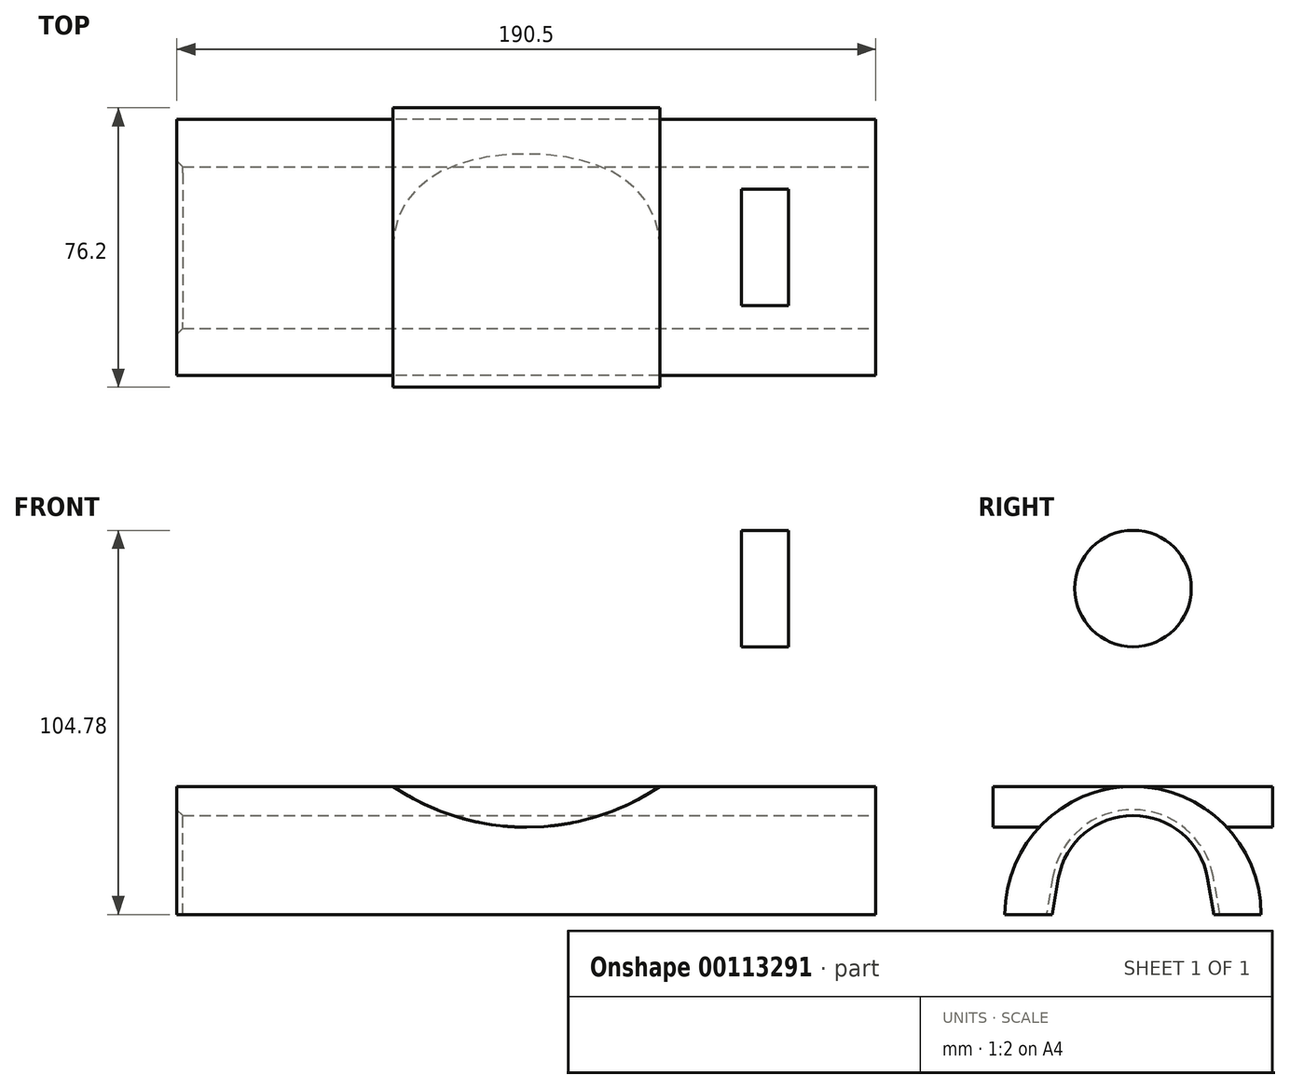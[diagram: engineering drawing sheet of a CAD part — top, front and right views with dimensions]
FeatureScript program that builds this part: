
annotation { "Feature Type Name" : "Feature", "Feature Type Description" : "" }
export const myFeature = defineFeature(function(context is Context, id is Id, definition is map)
    precondition{}
    {
        {
            var Q0;
            Q0=qCreatedBy(makeId("Top.planeOp"),FACE);
            var sketch = newSketch(context, id + "F0", { "sketchPlane" : qUnion([Q0])});
            skLineSegment(sketch, "E0.bottom", {"start": v(95.25, 34.92) * mm, "end": v(-95.25, 34.92) * mm});
            skLineSegment(sketch, "E0.top", {"start": v(95.25, -34.93) * mm, "end": v(-95.25, -34.93) * mm});
            skLineSegment(sketch, "E0.left", {"start": v(95.25, 34.93) * mm, "end": v(95.25, -34.93) * mm});
            skLineSegment(sketch, "E0.right", {"start": v(-95.25, 34.93) * mm, "end": v(-95.25, -34.93) * mm});
            skPoint(sketch, "E0.middle", {"position": v(0, 0) * mm});
            skSolve(sketch);
        }
        {
            var Q0;
            Q0=makeQuery(id+"F0.imprint","IMPRINT",FACE,{"disambiguationData":[TD([[makeQuery(id+"F0.imprint","IMPRINT",EDGE,{"derivedFrom":sQuery(id+"F0.wireOp",EDGE,"E0.bottom")}),1.0]])]});
            extrude(context, id + "F1", {"entities" : qUnion([Q0]), "depth" : 34.92 * mm});
        }
        {
            var Q0;
            Q0=makeQuery(id+"F1.opExtrude","SWEPT_FACE",FACE,{"disambiguationData":[OSD([sQuery(id+"F0.wireOp",EDGE,"E0.left")])]});
            var sketch = newSketch(context, id + "F2", { "sketchPlane" : qUnion([Q0])});
            skCircle(sketch, "E1", {"center": v(0, 0) * mm, "radius": 34.93 * mm});
            skSolve(sketch);
        }
        {
            var Q0;
            Q0=makeQuery(id+"F1.opExtrude","SWEPT_FACE",FACE,{"disambiguationData":[OSD([sQuery(id+"F0.wireOp",EDGE,"E0.top")])]});
            var sketch = newSketch(context, id + "F3", { "sketchPlane" : qUnion([Q0])});
            skLineSegment(sketch, "E2", {"start": v(0, 0) * mm, "end": v(0, 88.9) * mm});
            skCircle(sketch, "E3", {"center": v(0, 88.9) * mm, "radius": 65.09 * mm});
            skSolve(sketch);
        }
        {
            var Q0;
            {var subQ1=sQuery(id+"F0.wireOp",EDGE,"E0.left");var subQ2=makeQuery(id+"F1.opExtrude","SWEPT_EDGE",EDGE,{"disambiguationData":[OSD([sQuery(id+"F0.wireOp",EDGE,"E0.top"),subQ1])]});Q0=makeQuery(id+"F2.imprint","IMPRINT",FACE,{"disambiguationData":[TD([[makeQuery(id+"F2.imprint","IMPRINT",EDGE,{"derivedFrom":subQ2}),1.0]])]});}
            var Q1;
            {var subQ1=sQuery(id+"F0.wireOp",EDGE,"E0.left");var subQ2=makeQuery(id+"F1.opExtrude","SWEPT_EDGE",EDGE,{"disambiguationData":[OSD([sQuery(id+"F0.wireOp",EDGE,"E0.bottom"),subQ1])]});Q1=makeQuery(id+"F2.imprint","IMPRINT",FACE,{"disambiguationData":[TD([[makeQuery(id+"F2.imprint","IMPRINT",EDGE,{"derivedFrom":subQ2}),-1.0]])]});}
            extrude(context, id + "F4", {"entities" : qUnion([Q0, Q1]), "operationType" : NewBodyOperationType.REMOVE, "oppositeDirection" : true, "depth" : 190.5 * mm});
        }
        {
            var Q0;
            {var subQ0=sQuery(id+"F3.wireOp",EDGE,"E3");var subQ1=makeQuery(id+"F1.opExtrude","CAP_EDGE",EDGE,{"disambiguationData":[OSD([sQuery(id+"F0.wireOp",EDGE,"E0.top")])],"isStart":false});var subQ2=makeQuery(id+"F3.imprint","INTERSECT",VERTEX,{"disambiguationData":[OD(0.0)],"derivedFrom":[subQ1,subQ0]});Q0=makeQuery(id+"F3.imprint","IMPRINT",FACE,{"disambiguationData":[TD([[makeQuery(id+"F3.imprint","IMPRINT",EDGE,{"disambiguationData":[TD([[subQ2,1.0]])],"derivedFrom":subQ0}),1.0]])]});}
            var Q1;
            {var subQ0=sQuery(id+"F3.wireOp",EDGE,"E3");var subQ1=sQuery(id+"F3.wireOp",EDGE,"E2");var subQ2=makeQuery(id+"F3.imprint","INTERSECT",VERTEX,{"derivedFrom":[subQ1,subQ0]});Q1=makeQuery(id+"F3.imprint","IMPRINT",FACE,{"disambiguationData":[TD([[makeQuery(id+"F3.imprint","IMPRINT",EDGE,{"disambiguationData":[TD([[subQ2,-1.0]])],"derivedFrom":subQ1}),-1.0]])]});}
            var Q2;
            {var subQ0=sQuery(id+"F3.wireOp",EDGE,"E3");var subQ1=sQuery(id+"F3.wireOp",EDGE,"E2");var subQ2=makeQuery(id+"F3.imprint","INTERSECT",VERTEX,{"derivedFrom":[subQ1,subQ0]});Q2=makeQuery(id+"F3.imprint","IMPRINT",FACE,{"disambiguationData":[TD([[makeQuery(id+"F3.imprint","IMPRINT",EDGE,{"disambiguationData":[TD([[subQ2,-1.0]])],"derivedFrom":subQ1}),1.0]])]});}
            extrude(context, id + "F5", {"entities" : qUnion([Q0, Q1, Q2]), "operationType" : NewBodyOperationType.ADD, "oppositeDirection" : true, "depth" : 73.02 * mm});
        }
        {
            var Q0;
            Q0=makeQuery(id+"F5.opExtrude","CAP_FACE",FACE,{"disambiguationData":[OSD([sQuery(id+"F3.wireOp",EDGE,"E3")])],"isStart":true});
            extrude(context, id + "F6", {"entities" : qUnion([Q0]), "operationType" : NewBodyOperationType.ADD, "depth" : 3.17 * mm});
        }
        {
            var Q0;
            Q0=makeQuery(id+"F1.opExtrude","SWEPT_FACE",FACE,{"disambiguationData":[OSD([sQuery(id+"F0.wireOp",EDGE,"E0.left")])]});
            var sketch = newSketch(context, id + "F7", { "sketchPlane" : qUnion([Q0])});
            skPoint(sketch, "E4", {"position": v(0, 0) * mm});
            skSolve(sketch);
        }
        {
            var Q0;
            {var subQ0=sQuery(id+"F0.wireOp",EDGE,"E0.left");var subQ1=makeQuery(id+"F1.opExtrude","CAP_EDGE",EDGE,{"disambiguationData":[OSD([subQ0])],"isStart":true});Q0=makeQuery(id+"F7.imprint","IMPRINT",FACE,{"disambiguationData":[TD([[makeQuery(id+"F7.imprint","IMPRINT",EDGE,{"derivedFrom":subQ1}),-1.0]])]});}
            var sketch = newSketch(context, id + "F8", { "sketchPlane" : qUnion([Q0])});
            skPoint(sketch, "E5", {"position": v(0, 0) * mm});
            skLineSegment(sketch, "E6", {"start": v(0, 0) * mm, "end": v(0, 6.35) * mm});
            skArc(sketch, "E7", {"start": v(20.32, 9.93) * mm, "mid": v(0, 26.99) * mm, "end": v(-20.32, 9.93) * mm});
            skArc(sketch, "E8", {"start": v(22.67, 10.35) * mm, "mid": v(0, 29.37) * mm, "end": v(-22.67, 10.35) * mm});
            skLineSegment(sketch, "E9", {"start": v(-22.67, 10.35) * mm, "end": v(-24.5, 0) * mm});
            skLineSegment(sketch, "E10", {"start": v(-20.32, 9.93) * mm, "end": v(-22.08, 0) * mm});
            skLineSegment(sketch, "E11", {"start": v(22.67, 10.35) * mm, "end": v(24.5, 0) * mm});
            skLineSegment(sketch, "E12", {"start": v(20.32, 9.93) * mm, "end": v(22.08, 0) * mm});
            skLineSegment(sketch, "E13", {"start": v(-24.5, 0) * mm, "end": v(24.5, 0) * mm});
            skSolve(sketch);
        }
        {
            var Q0;
            Q0=makeQuery(id+"F8.imprint","IMPRINT",FACE,{"disambiguationData":[TD([[makeQuery(id+"F8.imprint","IMPRINT",EDGE,{"derivedFrom":sQuery(id+"F8.wireOp",EDGE,"E7")}),1.0]])]});
            extrude(context, id + "F9", {"entities" : qUnion([Q0]), "operationType" : NewBodyOperationType.REMOVE, "endBound" : BoundingType.THROUGH_ALL, "oppositeDirection" : true, "depth" : 25.4 * mm});
        }
        {
            var Q0;
            Q0=makeQuery(id+"F9.boolean.opBoolean","COPY",EDGE,{"derivedFrom":makeQuery(id+"F9.opExtrude","CAP_EDGE",EDGE,{"disambiguationData":[OSD([sQuery(id+"F8.wireOp",EDGE,"E7")])],"isStart":true})});
            var Q1;
            Q1=makeQuery(id+"F9.boolean.opBoolean","COPY",EDGE,{"derivedFrom":makeQuery(id+"F9.opExtrude","CAP_EDGE",EDGE,{"disambiguationData":[OSD([sQuery(id+"F8.wireOp",EDGE,"E12")])],"isStart":true})});
            var Q2;
            Q2=makeQuery(id+"F9.boolean.opBoolean","COPY",EDGE,{"derivedFrom":makeQuery(id+"F9.opExtrude","CAP_EDGE",EDGE,{"disambiguationData":[OSD([sQuery(id+"F8.wireOp",EDGE,"E10")])],"isStart":true})});
            var Q3;
            Q3=makeQuery(id+"F9.boolean.opBoolean","INTERSECT",EDGE,{"derivedFrom":[makeQuery(id+"F1.opExtrude","SWEPT_FACE",FACE,{"disambiguationData":[OSD([sQuery(id+"F0.wireOp",EDGE,"E0.right")])]}),makeQuery(id+"F9.opExtrude","SWEPT_FACE",FACE,{"disambiguationData":[OSD([sQuery(id+"F8.wireOp",EDGE,"E7")])]})]});
            var Q4;
            Q4=makeQuery(id+"F9.boolean.opBoolean","INTERSECT",EDGE,{"derivedFrom":[makeQuery(id+"F1.opExtrude","SWEPT_FACE",FACE,{"disambiguationData":[OSD([sQuery(id+"F0.wireOp",EDGE,"E0.right")])]}),makeQuery(id+"F9.opExtrude","SWEPT_FACE",FACE,{"disambiguationData":[OSD([sQuery(id+"F8.wireOp",EDGE,"E10")])]})]});
            var Q5;
            Q5=makeQuery(id+"F9.boolean.opBoolean","INTERSECT",EDGE,{"derivedFrom":[makeQuery(id+"F1.opExtrude","SWEPT_FACE",FACE,{"disambiguationData":[OSD([sQuery(id+"F0.wireOp",EDGE,"E0.right")])]}),makeQuery(id+"F9.opExtrude","SWEPT_FACE",FACE,{"disambiguationData":[OSD([sQuery(id+"F8.wireOp",EDGE,"E12")])]})]});
            chamfer(context, id + "F10", {"entities" : qUnion([Q0, Q1, Q2, Q3, Q4, Q5]), "chamferType" : ChamferType.OFFSET_ANGLE, "width" : 1.59 * mm, "oppositeDirection" : false, "angle" : 45 * degree, "tangentPropagation" : true});
        }
        {
            var Q0;
            Q0=makeQuery(id+"F5.opExtrude","CAP_FACE",FACE,{"disambiguationData":[OSD([sQuery(id+"F3.wireOp",EDGE,"E3")])],"isStart":false});
            var sketch = newSketch(context, id + "F11", { "sketchPlane" : qUnion([Q0])});
            skPoint(sketch, "E14", {"position": v(0, 88.9) * mm});
            skCircle(sketch, "E15", {"center": v(0, 88.9) * mm, "radius": 58.74 * mm});
            skSolve(sketch);
        }
        {
            var Q0;
            Q0=makeQuery(id+"F6.opExtrude","CAP_FACE",FACE,{"disambiguationData":[OSD([sQuery(id+"F3.wireOp",EDGE,"E3")])],"isStart":false});
            var sketch = newSketch(context, id + "F12", { "sketchPlane" : qUnion([Q0])});
            skLineSegment(sketch, "E16", {"start": v(0, 88.9) * mm, "end": v(134.94, 88.9) * mm});
            skCircle(sketch, "E17", {"center": v(134.94, 88.9) * mm, "radius": 63.5 * mm});
            skLineSegment(sketch, "E18", {"start": v(0, 0) * mm, "end": v(0, 34.93) * mm});
            skLineSegment(sketch, "E19.bottom", {"start": v(0, 34.93) * mm, "end": v(134.94, 34.93) * mm});
            skLineSegment(sketch, "E19.left", {"start": v(0, 34.93) * mm, "end": v(0, 88.9) * mm});
            skLineSegment(sketch, "E19.right", {"start": v(134.94, 34.93) * mm, "end": v(134.94, 88.9) * mm});
            skLineSegment(sketch, "E20.bottom", {"start": v(0, 153.99) * mm, "end": v(134.94, 153.99) * mm});
            skLineSegment(sketch, "E20.left", {"start": v(0, 153.99) * mm, "end": v(0, 88.9) * mm});
            skLineSegment(sketch, "E20.right", {"start": v(134.94, 153.99) * mm, "end": v(134.94, 88.9) * mm});
            skSolve(sketch);
        }
        {
            var Q0;
            {var subQ0=sQuery(id+"F0.wireOp",EDGE,"E0.left");var subQ1=makeQuery(id+"F1.opExtrude","CAP_EDGE",EDGE,{"disambiguationData":[OSD([subQ0])],"isStart":true});Q0=makeQuery(id+"F7.imprint","IMPRINT",FACE,{"disambiguationData":[TD([[makeQuery(id+"F7.imprint","IMPRINT",EDGE,{"derivedFrom":subQ1}),-1.0]])]});}
            var sketch = newSketch(context, id + "F13", { "sketchPlane" : qUnion([Q0])});
            skLineSegment(sketch, "E21", {"start": v(0, 0) * mm, "end": v(0, 88.9) * mm});
            skCircle(sketch, "E22", {"center": v(0, 88.9) * mm, "radius": 15.88 * mm});
            skSolve(sketch);
        }
        {
            var Q0;
            Q0=makeQuery(id+"F13.imprint","IMPRINT",FACE,{"disambiguationData":[TD([[makeQuery(id+"F13.imprint","IMPRINT",EDGE,{"derivedFrom":sQuery(id+"F13.wireOp",EDGE,"E22")}),1.0]])]});
            extrude(context, id + "F14", {"entities" : qUnion([Q0]), "operationType" : NewBodyOperationType.ADD, "oppositeDirection" : true, "depth" : 36.65 * mm});
        }
        {
            var Q0;
            Q0=makeQuery(id+"F12.imprint","IMPRINT",FACE,{"disambiguationData":[TD([[makeQuery(id+"F12.imprint","IMPRINT",EDGE,{"derivedFrom":makeQuery(id+"F6.opExtrude","CAP_EDGE",EDGE,{"disambiguationData":[OSD([sQuery(id+"F3.wireOp",EDGE,"E3")])],"isStart":false})}),1.0]])]});
            var sketch = newSketch(context, id + "F15", { "sketchPlane" : qUnion([Q0])});
            skLineSegment(sketch, "E23", {"start": v(0, 0) * mm, "end": v(0, 88.9) * mm});
            skLineSegment(sketch, "E24", {"start": v(0, 88.9) * mm, "end": v(65.09, 88.9) * mm});
            skLineSegment(sketch, "E25", {"start": v(65.09, 88.9) * mm, "end": v(71.44, 88.9) * mm});
            skLineSegment(sketch, "E26", {"start": v(71.44, 88.9) * mm, "end": v(71.44, 107.92) * mm});
            skLineSegment(sketch, "E27", {"start": v(71.44, 107.92) * mm, "end": v(71.44, 69.22) * mm});
            skLineSegment(sketch, "E28.bottom", {"start": v(71.44, 107.92) * mm, "end": v(104.9, 107.92) * mm});
            skLineSegment(sketch, "E28.top", {"start": v(71.44, 68.75) * mm, "end": v(104.9, 68.75) * mm});
            skLineSegment(sketch, "E28.left", {"start": v(71.44, 107.92) * mm, "end": v(71.44, 68.75) * mm});
            skLineSegment(sketch, "E28.right", {"start": v(104.9, 107.92) * mm, "end": v(104.9, 68.75) * mm});
            skSolve(sketch);
        }
        {
            var Q0;
            {var subQ4=sQuery(id+"F15.wireOp",EDGE,"E28.bottom");Q0=makeQuery(id+"F15.imprint","IMPRINT",FACE,{"disambiguationData":[TD([[makeQuery(id+"F15.imprint","IMPRINT",EDGE,{"derivedFrom":subQ4}),-1.0]])]});}
            extrude(context, id + "F16", {"entities" : qUnion([Q0]), "operationType" : NewBodyOperationType.REMOVE, "oppositeDirection" : true, "depth" : 83.55 * mm});
        }
        {
            var Q0;
            Q0=sQuery(id+"F11.wireOp",VERTEX,"E14");
            var Q1;
            Q1=makeQuery(id+"F1.opExtrude","SWEPT_BODY",BODY,{"disambiguationData":[OSD([sQuery(id+"F0.wireOp",EDGE,"E0.bottom"),sQuery(id+"F0.wireOp",EDGE,"E0.top"),sQuery(id+"F0.wireOp",EDGE,"E0.left"),sQuery(id+"F0.wireOp",EDGE,"E0.right")])]});
            hole(context, id + "F17", {"style" : HoleStyle.C_BORE, "endStyle" : HoleEndStyle.THROUGH, "holeDiameter" : 104.77 * mm, "cBoreDiameter" : 104.8 * mm, "cBoreDepth" : 6.35 * mm, "locations" : qUnion([Q0]), "scope" : qUnion([Q1]), "isTappedThrough" : true});
        }
    });
